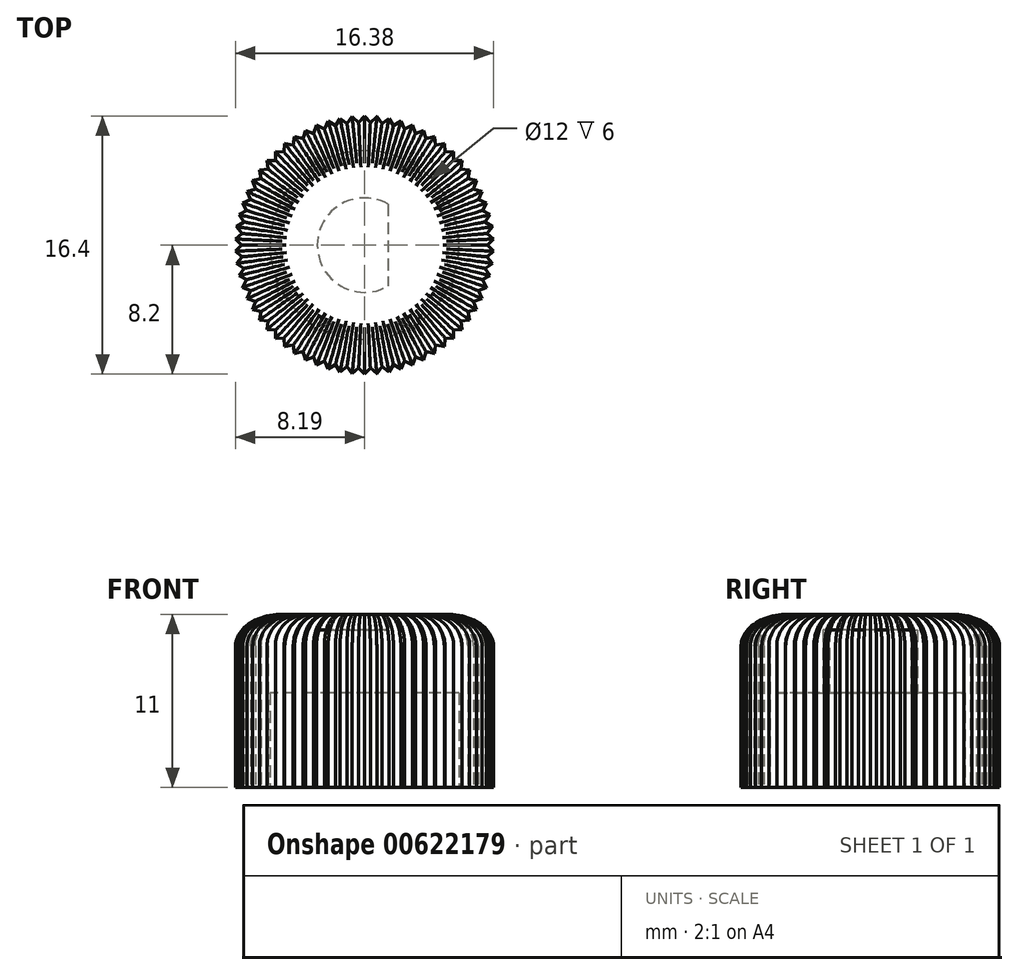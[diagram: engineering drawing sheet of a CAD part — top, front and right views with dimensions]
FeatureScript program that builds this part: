
annotation { "Feature Type Name" : "Feature", "Feature Type Description" : "" }
export const myFeature = defineFeature(function(context is Context, id is Id, definition is map)
    precondition{}
    {
        {
            var Q0;
            Q0=qCreatedBy(makeId("Top.planeOp"),FACE);
            var sketch = newSketch(context, id + "F0", { "sketchPlane" : qUnion([Q0])});
            skArc(sketch, "E0", {"start": v(1.5, 2.6) * mm, "mid": v(-3, 0) * mm, "end": v(1.5, -2.6) * mm});
            skLineSegment(sketch, "E1", {"start": v(1.5, 2.6) * mm, "end": v(1.5, -2.6) * mm});
            skCircle(sketch, "E2", {"center": v(0, 0) * mm, "radius": 8 * mm, "construction": true});
            skCircle(sketch, "E3.0", {"center": v(0, 0) * mm, "radius": 8.2 * mm, "construction": true});
            skCircle(sketch, "E4.0", {"center": v(0, 0) * mm, "radius": 7.8 * mm, "construction": true});
            skLineSegment(sketch, "E5", {"start": v(-7.8, 0) * mm, "end": v(-8.2, 0.4) * mm});
            skLineSegment(sketch, "E6", {"start": v(-7.8, 0) * mm, "end": v(-8.2, 0) * mm, "construction": true});
            skLineSegment(sketch, "E7", {"start": v(-7.8, 0) * mm, "end": v(-8.2, -0.4) * mm});
            skLineSegment(sketch, "E8.1.0", {"start": v(-7.76, -0.74) * mm, "end": v(-8.12, -1.17) * mm});
            skLineSegment(sketch, "E8.1.1", {"start": v(-7.76, -0.74) * mm, "end": v(-8.2, -0.39) * mm});
            skLineSegment(sketch, "E8.2.0", {"start": v(-7.66, -1.48) * mm, "end": v(-7.97, -1.93) * mm});
            skLineSegment(sketch, "E8.2.1", {"start": v(-7.66, -1.48) * mm, "end": v(-8.12, -1.17) * mm});
            skLineSegment(sketch, "E8.3.0", {"start": v(-7.48, -2.2) * mm, "end": v(-7.75, -2.68) * mm});
            skLineSegment(sketch, "E8.3.1", {"start": v(-7.48, -2.2) * mm, "end": v(-7.97, -1.93) * mm});
            skLineSegment(sketch, "E8.4.0", {"start": v(-7.24, -2.9) * mm, "end": v(-7.46, -3.4) * mm});
            skLineSegment(sketch, "E8.4.1", {"start": v(-7.24, -2.9) * mm, "end": v(-7.75, -2.68) * mm});
            skLineSegment(sketch, "E8.5.0", {"start": v(-6.93, -3.57) * mm, "end": v(-7.1, -4.1) * mm});
            skLineSegment(sketch, "E8.5.1", {"start": v(-6.93, -3.57) * mm, "end": v(-7.46, -3.4) * mm});
            skLineSegment(sketch, "E8.6.0", {"start": v(-6.56, -4.22) * mm, "end": v(-6.68, -4.76) * mm});
            skLineSegment(sketch, "E8.6.1", {"start": v(-6.56, -4.22) * mm, "end": v(-7.1, -4.1) * mm});
            skLineSegment(sketch, "E8.7.0", {"start": v(-6.13, -4.82) * mm, "end": v(-6.2, -5.37) * mm});
            skLineSegment(sketch, "E8.7.1", {"start": v(-6.13, -4.82) * mm, "end": v(-6.68, -4.76) * mm});
            skLineSegment(sketch, "E8.8.0", {"start": v(-5.65, -5.38) * mm, "end": v(-5.66, -5.93) * mm});
            skLineSegment(sketch, "E8.8.1", {"start": v(-5.65, -5.38) * mm, "end": v(-6.2, -5.37) * mm});
            skLineSegment(sketch, "E8.9.0", {"start": v(-5.1, -5.9) * mm, "end": v(-5.07, -6.45) * mm});
            skLineSegment(sketch, "E8.9.1", {"start": v(-5.1, -5.9) * mm, "end": v(-5.66, -5.93) * mm});
            skLineSegment(sketch, "E8.10.0", {"start": v(-4.52, -6.35) * mm, "end": v(-4.43, -6.9) * mm});
            skLineSegment(sketch, "E8.10.1", {"start": v(-4.52, -6.35) * mm, "end": v(-5.07, -6.45) * mm});
            skLineSegment(sketch, "E8.11.0", {"start": v(-3.9, -6.75) * mm, "end": v(-3.76, -7.29) * mm});
            skLineSegment(sketch, "E8.11.1", {"start": v(-3.9, -6.75) * mm, "end": v(-4.43, -6.9) * mm});
            skLineSegment(sketch, "E8.12.0", {"start": v(-3.24, -7.1) * mm, "end": v(-3.05, -7.61) * mm});
            skLineSegment(sketch, "E8.12.1", {"start": v(-3.24, -7.1) * mm, "end": v(-3.76, -7.29) * mm});
            skLineSegment(sketch, "E8.13.0", {"start": v(-2.55, -7.37) * mm, "end": v(-2.3, -7.87) * mm});
            skLineSegment(sketch, "E8.13.1", {"start": v(-2.55, -7.37) * mm, "end": v(-3.05, -7.61) * mm});
            skLineSegment(sketch, "E8.14.0", {"start": v(-1.84, -7.58) * mm, "end": v(-1.55, -8.05) * mm});
            skLineSegment(sketch, "E8.14.1", {"start": v(-1.84, -7.58) * mm, "end": v(-2.31, -7.87) * mm});
            skLineSegment(sketch, "E8.15.0", {"start": v(-1.11, -7.72) * mm, "end": v(-0.78, -8.16) * mm});
            skLineSegment(sketch, "E8.15.1", {"start": v(-1.11, -7.72) * mm, "end": v(-1.55, -8.05) * mm});
            skLineSegment(sketch, "E8.16.0", {"start": v(-0.37, -7.8) * mm, "end": v(0, -8.2) * mm});
            skLineSegment(sketch, "E8.16.1", {"start": v(-0.37, -7.8) * mm, "end": v(-0.78, -8.16) * mm});
            skLineSegment(sketch, "E8.17.0", {"start": v(0.37, -7.8) * mm, "end": v(0.78, -8.16) * mm});
            skLineSegment(sketch, "E8.17.1", {"start": v(0.37, -7.8) * mm, "end": v(0, -8.2) * mm});
            skLineSegment(sketch, "E8.18.0", {"start": v(1.11, -7.72) * mm, "end": v(1.55, -8.05) * mm});
            skLineSegment(sketch, "E8.18.1", {"start": v(1.11, -7.72) * mm, "end": v(0.78, -8.16) * mm});
            skLineSegment(sketch, "E8.19.0", {"start": v(1.84, -7.58) * mm, "end": v(2.31, -7.87) * mm});
            skLineSegment(sketch, "E8.19.1", {"start": v(1.84, -7.58) * mm, "end": v(1.55, -8.05) * mm});
            skLineSegment(sketch, "E8.20.0", {"start": v(2.55, -7.37) * mm, "end": v(3.05, -7.61) * mm});
            skLineSegment(sketch, "E8.20.1", {"start": v(2.55, -7.37) * mm, "end": v(2.3, -7.87) * mm});
            skLineSegment(sketch, "E8.21.0", {"start": v(3.24, -7.1) * mm, "end": v(3.76, -7.29) * mm});
            skLineSegment(sketch, "E8.21.1", {"start": v(3.24, -7.1) * mm, "end": v(3.05, -7.61) * mm});
            skLineSegment(sketch, "E8.22.0", {"start": v(3.9, -6.75) * mm, "end": v(4.43, -6.9) * mm});
            skLineSegment(sketch, "E8.22.1", {"start": v(3.9, -6.75) * mm, "end": v(3.76, -7.29) * mm});
            skLineSegment(sketch, "E8.23.0", {"start": v(4.52, -6.35) * mm, "end": v(5.07, -6.45) * mm});
            skLineSegment(sketch, "E8.23.1", {"start": v(4.52, -6.35) * mm, "end": v(4.43, -6.9) * mm});
            skLineSegment(sketch, "E8.24.0", {"start": v(5.1, -5.9) * mm, "end": v(5.66, -5.93) * mm});
            skLineSegment(sketch, "E8.24.1", {"start": v(5.1, -5.9) * mm, "end": v(5.07, -6.45) * mm});
            skLineSegment(sketch, "E8.25.0", {"start": v(5.65, -5.38) * mm, "end": v(6.2, -5.37) * mm});
            skLineSegment(sketch, "E8.25.1", {"start": v(5.65, -5.38) * mm, "end": v(5.66, -5.93) * mm});
            skLineSegment(sketch, "E8.26.0", {"start": v(6.13, -4.82) * mm, "end": v(6.68, -4.76) * mm});
            skLineSegment(sketch, "E8.26.1", {"start": v(6.13, -4.82) * mm, "end": v(6.2, -5.37) * mm});
            skLineSegment(sketch, "E8.27.0", {"start": v(6.56, -4.22) * mm, "end": v(7.1, -4.1) * mm});
            skLineSegment(sketch, "E8.27.1", {"start": v(6.56, -4.22) * mm, "end": v(6.68, -4.76) * mm});
            skLineSegment(sketch, "E8.28.0", {"start": v(6.93, -3.57) * mm, "end": v(7.46, -3.4) * mm});
            skLineSegment(sketch, "E8.28.1", {"start": v(6.93, -3.57) * mm, "end": v(7.1, -4.1) * mm});
            skLineSegment(sketch, "E8.29.0", {"start": v(7.24, -2.9) * mm, "end": v(7.75, -2.68) * mm});
            skLineSegment(sketch, "E8.29.1", {"start": v(7.24, -2.9) * mm, "end": v(7.46, -3.4) * mm});
            skLineSegment(sketch, "E8.30.0", {"start": v(7.48, -2.2) * mm, "end": v(7.97, -1.93) * mm});
            skLineSegment(sketch, "E8.30.1", {"start": v(7.48, -2.2) * mm, "end": v(7.75, -2.68) * mm});
            skLineSegment(sketch, "E8.31.0", {"start": v(7.66, -1.48) * mm, "end": v(8.12, -1.17) * mm});
            skLineSegment(sketch, "E8.31.1", {"start": v(7.66, -1.48) * mm, "end": v(7.97, -1.93) * mm});
            skLineSegment(sketch, "E8.32.0", {"start": v(7.76, -0.74) * mm, "end": v(8.2, -0.39) * mm});
            skLineSegment(sketch, "E8.32.1", {"start": v(7.76, -0.74) * mm, "end": v(8.12, -1.17) * mm});
            skLineSegment(sketch, "E8.33.0", {"start": v(7.8, 0) * mm, "end": v(8.2, 0.4) * mm});
            skLineSegment(sketch, "E8.33.1", {"start": v(7.8, 0) * mm, "end": v(8.2, -0.4) * mm});
            skLineSegment(sketch, "E8.34.0", {"start": v(7.76, 0.74) * mm, "end": v(8.12, 1.17) * mm});
            skLineSegment(sketch, "E8.34.1", {"start": v(7.76, 0.74) * mm, "end": v(8.2, 0.39) * mm});
            skLineSegment(sketch, "E8.35.0", {"start": v(7.66, 1.48) * mm, "end": v(7.97, 1.93) * mm});
            skLineSegment(sketch, "E8.35.1", {"start": v(7.66, 1.48) * mm, "end": v(8.12, 1.17) * mm});
            skLineSegment(sketch, "E8.36.0", {"start": v(7.48, 2.2) * mm, "end": v(7.75, 2.68) * mm});
            skLineSegment(sketch, "E8.36.1", {"start": v(7.48, 2.2) * mm, "end": v(7.97, 1.93) * mm});
            skLineSegment(sketch, "E8.37.0", {"start": v(7.24, 2.9) * mm, "end": v(7.46, 3.4) * mm});
            skLineSegment(sketch, "E8.37.1", {"start": v(7.24, 2.9) * mm, "end": v(7.75, 2.68) * mm});
            skLineSegment(sketch, "E8.38.0", {"start": v(6.93, 3.57) * mm, "end": v(7.1, 4.1) * mm});
            skLineSegment(sketch, "E8.38.1", {"start": v(6.93, 3.57) * mm, "end": v(7.46, 3.4) * mm});
            skLineSegment(sketch, "E8.39.0", {"start": v(6.56, 4.22) * mm, "end": v(6.68, 4.76) * mm});
            skLineSegment(sketch, "E8.39.1", {"start": v(6.56, 4.22) * mm, "end": v(7.1, 4.1) * mm});
            skLineSegment(sketch, "E8.40.0", {"start": v(6.13, 4.82) * mm, "end": v(6.2, 5.37) * mm});
            skLineSegment(sketch, "E8.40.1", {"start": v(6.13, 4.82) * mm, "end": v(6.68, 4.76) * mm});
            skLineSegment(sketch, "E8.41.0", {"start": v(5.65, 5.38) * mm, "end": v(5.66, 5.93) * mm});
            skLineSegment(sketch, "E8.41.1", {"start": v(5.65, 5.38) * mm, "end": v(6.2, 5.37) * mm});
            skLineSegment(sketch, "E8.42.0", {"start": v(5.1, 5.9) * mm, "end": v(5.07, 6.45) * mm});
            skLineSegment(sketch, "E8.42.1", {"start": v(5.1, 5.9) * mm, "end": v(5.66, 5.93) * mm});
            skLineSegment(sketch, "E8.43.0", {"start": v(4.52, 6.35) * mm, "end": v(4.43, 6.9) * mm});
            skLineSegment(sketch, "E8.43.1", {"start": v(4.52, 6.35) * mm, "end": v(5.07, 6.45) * mm});
            skLineSegment(sketch, "E8.44.0", {"start": v(3.9, 6.75) * mm, "end": v(3.76, 7.29) * mm});
            skLineSegment(sketch, "E8.44.1", {"start": v(3.9, 6.75) * mm, "end": v(4.43, 6.9) * mm});
            skLineSegment(sketch, "E8.45.0", {"start": v(3.24, 7.1) * mm, "end": v(3.05, 7.61) * mm});
            skLineSegment(sketch, "E8.45.1", {"start": v(3.24, 7.1) * mm, "end": v(3.76, 7.29) * mm});
            skLineSegment(sketch, "E8.46.0", {"start": v(2.55, 7.37) * mm, "end": v(2.3, 7.87) * mm});
            skLineSegment(sketch, "E8.46.1", {"start": v(2.55, 7.37) * mm, "end": v(3.05, 7.61) * mm});
            skLineSegment(sketch, "E8.47.0", {"start": v(1.84, 7.58) * mm, "end": v(1.55, 8.05) * mm});
            skLineSegment(sketch, "E8.47.1", {"start": v(1.84, 7.58) * mm, "end": v(2.31, 7.87) * mm});
            skLineSegment(sketch, "E8.48.0", {"start": v(1.11, 7.72) * mm, "end": v(0.78, 8.16) * mm});
            skLineSegment(sketch, "E8.48.1", {"start": v(1.11, 7.72) * mm, "end": v(1.55, 8.05) * mm});
            skLineSegment(sketch, "E8.49.0", {"start": v(0.37, 7.8) * mm, "end": v(0, 8.2) * mm});
            skLineSegment(sketch, "E8.49.1", {"start": v(0.37, 7.8) * mm, "end": v(0.78, 8.16) * mm});
            skCircle(sketch, "E9", {"center": v(0, 0) * mm, "radius": 6 * mm});
            skLineSegment(sketch, "E10.2.50.0", {"start": v(-0.37, 7.8) * mm, "end": v(-0.78, 8.16) * mm});
            skLineSegment(sketch, "E10.3.50.0", {"start": v(-0.37, 7.8) * mm, "end": v(0, 8.2) * mm});
            skLineSegment(sketch, "E10.2.51.0", {"start": v(-1.11, 7.72) * mm, "end": v(-1.55, 8.05) * mm});
            skLineSegment(sketch, "E10.3.51.0", {"start": v(-1.11, 7.72) * mm, "end": v(-0.78, 8.16) * mm});
            skLineSegment(sketch, "E10.2.52.0", {"start": v(-1.84, 7.58) * mm, "end": v(-2.31, 7.87) * mm});
            skLineSegment(sketch, "E10.3.52.0", {"start": v(-1.84, 7.58) * mm, "end": v(-1.55, 8.05) * mm});
            skLineSegment(sketch, "E10.2.53.0", {"start": v(-2.55, 7.37) * mm, "end": v(-3.05, 7.61) * mm});
            skLineSegment(sketch, "E10.3.53.0", {"start": v(-2.55, 7.37) * mm, "end": v(-2.3, 7.87) * mm});
            skLineSegment(sketch, "E10.2.54.0", {"start": v(-3.24, 7.1) * mm, "end": v(-3.76, 7.29) * mm});
            skLineSegment(sketch, "E10.3.54.0", {"start": v(-3.24, 7.1) * mm, "end": v(-3.05, 7.61) * mm});
            skLineSegment(sketch, "E10.2.55.0", {"start": v(-3.9, 6.75) * mm, "end": v(-4.43, 6.9) * mm});
            skLineSegment(sketch, "E10.3.55.0", {"start": v(-3.9, 6.75) * mm, "end": v(-3.76, 7.29) * mm});
            skLineSegment(sketch, "E10.2.56.0", {"start": v(-4.52, 6.35) * mm, "end": v(-5.07, 6.45) * mm});
            skLineSegment(sketch, "E10.3.56.0", {"start": v(-4.52, 6.35) * mm, "end": v(-4.43, 6.9) * mm});
            skLineSegment(sketch, "E10.2.57.0", {"start": v(-5.1, 5.9) * mm, "end": v(-5.66, 5.93) * mm});
            skLineSegment(sketch, "E10.3.57.0", {"start": v(-5.1, 5.9) * mm, "end": v(-5.07, 6.45) * mm});
            skLineSegment(sketch, "E10.2.58.0", {"start": v(-5.65, 5.38) * mm, "end": v(-6.2, 5.37) * mm});
            skLineSegment(sketch, "E10.3.58.0", {"start": v(-5.65, 5.38) * mm, "end": v(-5.66, 5.93) * mm});
            skLineSegment(sketch, "E10.2.59.0", {"start": v(-6.13, 4.82) * mm, "end": v(-6.68, 4.76) * mm});
            skLineSegment(sketch, "E10.3.59.0", {"start": v(-6.13, 4.82) * mm, "end": v(-6.2, 5.37) * mm});
            skLineSegment(sketch, "E11.2.60.0", {"start": v(-6.56, 4.22) * mm, "end": v(-7.1, 4.1) * mm});
            skLineSegment(sketch, "E11.3.60.0", {"start": v(-6.56, 4.22) * mm, "end": v(-6.68, 4.76) * mm});
            skLineSegment(sketch, "E11.2.61.0", {"start": v(-6.93, 3.57) * mm, "end": v(-7.46, 3.4) * mm});
            skLineSegment(sketch, "E11.3.61.0", {"start": v(-6.93, 3.57) * mm, "end": v(-7.1, 4.1) * mm});
            skLineSegment(sketch, "E11.2.62.0", {"start": v(-7.24, 2.9) * mm, "end": v(-7.75, 2.68) * mm});
            skLineSegment(sketch, "E11.3.62.0", {"start": v(-7.24, 2.9) * mm, "end": v(-7.46, 3.4) * mm});
            skLineSegment(sketch, "E11.2.63.0", {"start": v(-7.48, 2.2) * mm, "end": v(-7.97, 1.93) * mm});
            skLineSegment(sketch, "E11.3.63.0", {"start": v(-7.48, 2.2) * mm, "end": v(-7.75, 2.68) * mm});
            skLineSegment(sketch, "E11.2.64.0", {"start": v(-7.66, 1.48) * mm, "end": v(-8.12, 1.17) * mm});
            skLineSegment(sketch, "E11.3.64.0", {"start": v(-7.66, 1.48) * mm, "end": v(-7.97, 1.93) * mm});
            skLineSegment(sketch, "E12.2.65.0", {"start": v(-7.76, 0.74) * mm, "end": v(-8.2, 0.39) * mm});
            skLineSegment(sketch, "E12.3.65.0", {"start": v(-7.76, 0.74) * mm, "end": v(-8.12, 1.17) * mm});
            skCircle(sketch, "E13", {"center": v(0, 0) * mm, "radius": 4 * mm});
            skSolve(sketch);
        }
        {
            var Q0;
            Q0=makeQuery(id+"F0.imprint","IMPRINT",FACE,{"disambiguationData":[TD([[makeQuery(id+"F0.imprint","IMPRINT",EDGE,{"derivedFrom":sQuery(id+"F0.wireOp",EDGE,"E9")}),-1.0]])]});
            extrude(context, id + "F1", {"entities" : qUnion([Q0]), "depth" : 12 * mm, "offsetDistance" : 25 * mm, "hasSecondDirection" : true, "secondDirectionOppositeDirection" : false, "secondDirectionDepth" : 1 * mm});
        }
        {
            var Q0;
            Q0=makeQuery(id+"F0.imprint","IMPRINT",FACE,{"disambiguationData":[TD([[makeQuery(id+"F0.imprint","IMPRINT",EDGE,{"derivedFrom":sQuery(id+"F0.wireOp",EDGE,"E0")}),-1.0]])]});
            var Q1;
            Q1=makeQuery(id+"F0.imprint","IMPRINT",FACE,{"disambiguationData":[TD([[makeQuery(id+"F0.imprint","IMPRINT",EDGE,{"derivedFrom":sQuery(id+"F0.wireOp",EDGE,"E9")}),1.0]])]});
            extrude(context, id + "F2", {"entities" : qUnion([Q0, Q1]), "operationType" : NewBodyOperationType.ADD, "depth" : 12 * mm, "offsetDistance" : 25 * mm, "hasSecondDirection" : true, "secondDirectionOppositeDirection" : false, "secondDirectionDepth" : 7 * mm});
        }
        {
            var Q0;
            Q0=makeQuery(id+"F0.imprint","IMPRINT",FACE,{"disambiguationData":[TD([[makeQuery(id+"F0.imprint","IMPRINT",EDGE,{"derivedFrom":sQuery(id+"F0.wireOp",EDGE,"E0")}),1.0]])]});
            extrude(context, id + "F3", {"entities" : qUnion([Q0]), "operationType" : NewBodyOperationType.ADD, "depth" : 12 * mm, "offsetDistance" : 25 * mm, "hasSecondDirection" : true, "secondDirectionOppositeDirection" : false, "secondDirectionDepth" : 11 * mm});
        }
        {
            var Q0;
            {var subQ0=sQuery(id+"F0.wireOp",EDGE,"E1");var subQ1=sQuery(id+"F0.wireOp",EDGE,"E0");var subQ2=sQuery(id+"F0.wireOp",EDGE,"E9");Q0=makeQuery(id+"F3.boolean.opBoolean","MERGE",FACE,{"derivedFrom":[makeQuery(id+"F2.boolean.opBoolean","MERGE",FACE,{"derivedFrom":[makeQuery(id+"F1.opExtrude","CAP_FACE",FACE,{"disambiguationData":[OSD([sQuery(id+"F0.wireOp",EDGE,"E5"),sQuery(id+"F0.wireOp",EDGE,"E7"),sQuery(id+"F0.wireOp",EDGE,"E8.1.0"),sQuery(id+"F0.wireOp",EDGE,"E8.1.1"),sQuery(id+"F0.wireOp",EDGE,"E8.2.0"),sQuery(id+"F0.wireOp",EDGE,"E8.2.1"),sQuery(id+"F0.wireOp",EDGE,"E8.3.0"),sQuery(id+"F0.wireOp",EDGE,"E8.3.1"),sQuery(id+"F0.wireOp",EDGE,"E8.4.0"),sQuery(id+"F0.wireOp",EDGE,"E8.4.1"),sQuery(id+"F0.wireOp",EDGE,"E8.5.0"),sQuery(id+"F0.wireOp",EDGE,"E8.5.1"),sQuery(id+"F0.wireOp",EDGE,"E8.6.0"),sQuery(id+"F0.wireOp",EDGE,"E8.6.1"),sQuery(id+"F0.wireOp",EDGE,"E8.7.0"),sQuery(id+"F0.wireOp",EDGE,"E8.7.1"),sQuery(id+"F0.wireOp",EDGE,"E8.8.0"),sQuery(id+"F0.wireOp",EDGE,"E8.8.1"),sQuery(id+"F0.wireOp",EDGE,"E8.9.0"),sQuery(id+"F0.wireOp",EDGE,"E8.9.1"),sQuery(id+"F0.wireOp",EDGE,"E8.10.0"),sQuery(id+"F0.wireOp",EDGE,"E8.10.1"),sQuery(id+"F0.wireOp",EDGE,"E8.11.0"),sQuery(id+"F0.wireOp",EDGE,"E8.11.1"),sQuery(id+"F0.wireOp",EDGE,"E8.12.0"),sQuery(id+"F0.wireOp",EDGE,"E8.12.1"),sQuery(id+"F0.wireOp",EDGE,"E8.13.0"),sQuery(id+"F0.wireOp",EDGE,"E8.13.1"),sQuery(id+"F0.wireOp",EDGE,"E8.14.0"),sQuery(id+"F0.wireOp",EDGE,"E8.14.1"),sQuery(id+"F0.wireOp",EDGE,"E8.15.0"),sQuery(id+"F0.wireOp",EDGE,"E8.15.1"),sQuery(id+"F0.wireOp",EDGE,"E8.16.0"),sQuery(id+"F0.wireOp",EDGE,"E8.16.1"),sQuery(id+"F0.wireOp",EDGE,"E8.17.0"),sQuery(id+"F0.wireOp",EDGE,"E8.17.1"),sQuery(id+"F0.wireOp",EDGE,"E8.18.0"),sQuery(id+"F0.wireOp",EDGE,"E8.18.1"),sQuery(id+"F0.wireOp",EDGE,"E8.19.0"),sQuery(id+"F0.wireOp",EDGE,"E8.19.1"),sQuery(id+"F0.wireOp",EDGE,"E8.20.0"),sQuery(id+"F0.wireOp",EDGE,"E8.20.1"),sQuery(id+"F0.wireOp",EDGE,"E8.21.0"),sQuery(id+"F0.wireOp",EDGE,"E8.21.1"),sQuery(id+"F0.wireOp",EDGE,"E8.22.0"),sQuery(id+"F0.wireOp",EDGE,"E8.22.1"),sQuery(id+"F0.wireOp",EDGE,"E8.23.0"),sQuery(id+"F0.wireOp",EDGE,"E8.23.1"),sQuery(id+"F0.wireOp",EDGE,"E8.24.0"),sQuery(id+"F0.wireOp",EDGE,"E8.24.1"),sQuery(id+"F0.wireOp",EDGE,"E8.25.0"),sQuery(id+"F0.wireOp",EDGE,"E8.25.1"),sQuery(id+"F0.wireOp",EDGE,"E8.26.0"),sQuery(id+"F0.wireOp",EDGE,"E8.26.1"),sQuery(id+"F0.wireOp",EDGE,"E8.27.0"),sQuery(id+"F0.wireOp",EDGE,"E8.27.1"),sQuery(id+"F0.wireOp",EDGE,"E8.28.0"),sQuery(id+"F0.wireOp",EDGE,"E8.28.1"),sQuery(id+"F0.wireOp",EDGE,"E8.29.0"),sQuery(id+"F0.wireOp",EDGE,"E8.29.1"),sQuery(id+"F0.wireOp",EDGE,"E8.30.0"),sQuery(id+"F0.wireOp",EDGE,"E8.30.1"),sQuery(id+"F0.wireOp",EDGE,"E8.31.0"),sQuery(id+"F0.wireOp",EDGE,"E8.31.1"),sQuery(id+"F0.wireOp",EDGE,"E8.32.0"),sQuery(id+"F0.wireOp",EDGE,"E8.32.1"),sQuery(id+"F0.wireOp",EDGE,"E8.33.0"),sQuery(id+"F0.wireOp",EDGE,"E8.33.1"),sQuery(id+"F0.wireOp",EDGE,"E8.34.0"),sQuery(id+"F0.wireOp",EDGE,"E8.34.1"),sQuery(id+"F0.wireOp",EDGE,"E8.35.0"),sQuery(id+"F0.wireOp",EDGE,"E8.35.1"),sQuery(id+"F0.wireOp",EDGE,"E8.36.0"),sQuery(id+"F0.wireOp",EDGE,"E8.36.1"),sQuery(id+"F0.wireOp",EDGE,"E8.37.0"),sQuery(id+"F0.wireOp",EDGE,"E8.37.1"),sQuery(id+"F0.wireOp",EDGE,"E8.38.0"),sQuery(id+"F0.wireOp",EDGE,"E8.38.1"),sQuery(id+"F0.wireOp",EDGE,"E8.39.0"),sQuery(id+"F0.wireOp",EDGE,"E8.39.1"),sQuery(id+"F0.wireOp",EDGE,"E8.40.0"),sQuery(id+"F0.wireOp",EDGE,"E8.40.1"),sQuery(id+"F0.wireOp",EDGE,"E8.41.0"),sQuery(id+"F0.wireOp",EDGE,"E8.41.1"),sQuery(id+"F0.wireOp",EDGE,"E8.42.0"),sQuery(id+"F0.wireOp",EDGE,"E8.42.1"),sQuery(id+"F0.wireOp",EDGE,"E8.43.0"),sQuery(id+"F0.wireOp",EDGE,"E8.43.1"),sQuery(id+"F0.wireOp",EDGE,"E8.44.0"),sQuery(id+"F0.wireOp",EDGE,"E8.44.1"),sQuery(id+"F0.wireOp",EDGE,"E8.45.0"),sQuery(id+"F0.wireOp",EDGE,"E8.45.1"),sQuery(id+"F0.wireOp",EDGE,"E8.46.0"),sQuery(id+"F0.wireOp",EDGE,"E8.46.1"),sQuery(id+"F0.wireOp",EDGE,"E8.47.0"),sQuery(id+"F0.wireOp",EDGE,"E8.47.1"),sQuery(id+"F0.wireOp",EDGE,"E8.48.0"),sQuery(id+"F0.wireOp",EDGE,"E8.48.1"),sQuery(id+"F0.wireOp",EDGE,"E8.49.0"),sQuery(id+"F0.wireOp",EDGE,"E8.49.1"),subQ2,sQuery(id+"F0.wireOp",EDGE,"E10.2.50.0"),sQuery(id+"F0.wireOp",EDGE,"E10.3.50.0"),sQuery(id+"F0.wireOp",EDGE,"E10.2.51.0"),sQuery(id+"F0.wireOp",EDGE,"E10.3.51.0"),sQuery(id+"F0.wireOp",EDGE,"E10.2.52.0"),sQuery(id+"F0.wireOp",EDGE,"E10.3.52.0"),sQuery(id+"F0.wireOp",EDGE,"E10.2.53.0"),sQuery(id+"F0.wireOp",EDGE,"E10.3.53.0"),sQuery(id+"F0.wireOp",EDGE,"E10.2.54.0"),sQuery(id+"F0.wireOp",EDGE,"E10.3.54.0"),sQuery(id+"F0.wireOp",EDGE,"E10.2.55.0"),sQuery(id+"F0.wireOp",EDGE,"E10.3.55.0"),sQuery(id+"F0.wireOp",EDGE,"E10.2.56.0"),sQuery(id+"F0.wireOp",EDGE,"E10.3.56.0"),sQuery(id+"F0.wireOp",EDGE,"E10.2.57.0"),sQuery(id+"F0.wireOp",EDGE,"E10.3.57.0"),sQuery(id+"F0.wireOp",EDGE,"E10.2.58.0"),sQuery(id+"F0.wireOp",EDGE,"E10.3.58.0"),sQuery(id+"F0.wireOp",EDGE,"E10.2.59.0"),sQuery(id+"F0.wireOp",EDGE,"E10.3.59.0"),sQuery(id+"F0.wireOp",EDGE,"E11.2.60.0"),sQuery(id+"F0.wireOp",EDGE,"E11.3.60.0"),sQuery(id+"F0.wireOp",EDGE,"E11.2.61.0"),sQuery(id+"F0.wireOp",EDGE,"E11.3.61.0"),sQuery(id+"F0.wireOp",EDGE,"E11.2.62.0"),sQuery(id+"F0.wireOp",EDGE,"E11.3.62.0"),sQuery(id+"F0.wireOp",EDGE,"E11.2.63.0"),sQuery(id+"F0.wireOp",EDGE,"E11.3.63.0"),sQuery(id+"F0.wireOp",EDGE,"E11.2.64.0"),sQuery(id+"F0.wireOp",EDGE,"E11.3.64.0"),sQuery(id+"F0.wireOp",EDGE,"E12.2.65.0"),sQuery(id+"F0.wireOp",EDGE,"E12.3.65.0")])],"isStart":false}),makeQuery(id+"F2.opExtrude","CAP_FACE",FACE,{"disambiguationData":[OSD([subQ1,subQ0,subQ2])],"isStart":false})]}),makeQuery(id+"F3.opExtrude","CAP_FACE",FACE,{"disambiguationData":[OSD([subQ1,subQ0])],"isStart":false})]});}
            fillet(context, id + "F4", {"entities" : qUnion([Q0]), "radius" : 2 * mm, "tangentPropagation" : true, "allowEdgeOverflow" : false});
        }
    });
